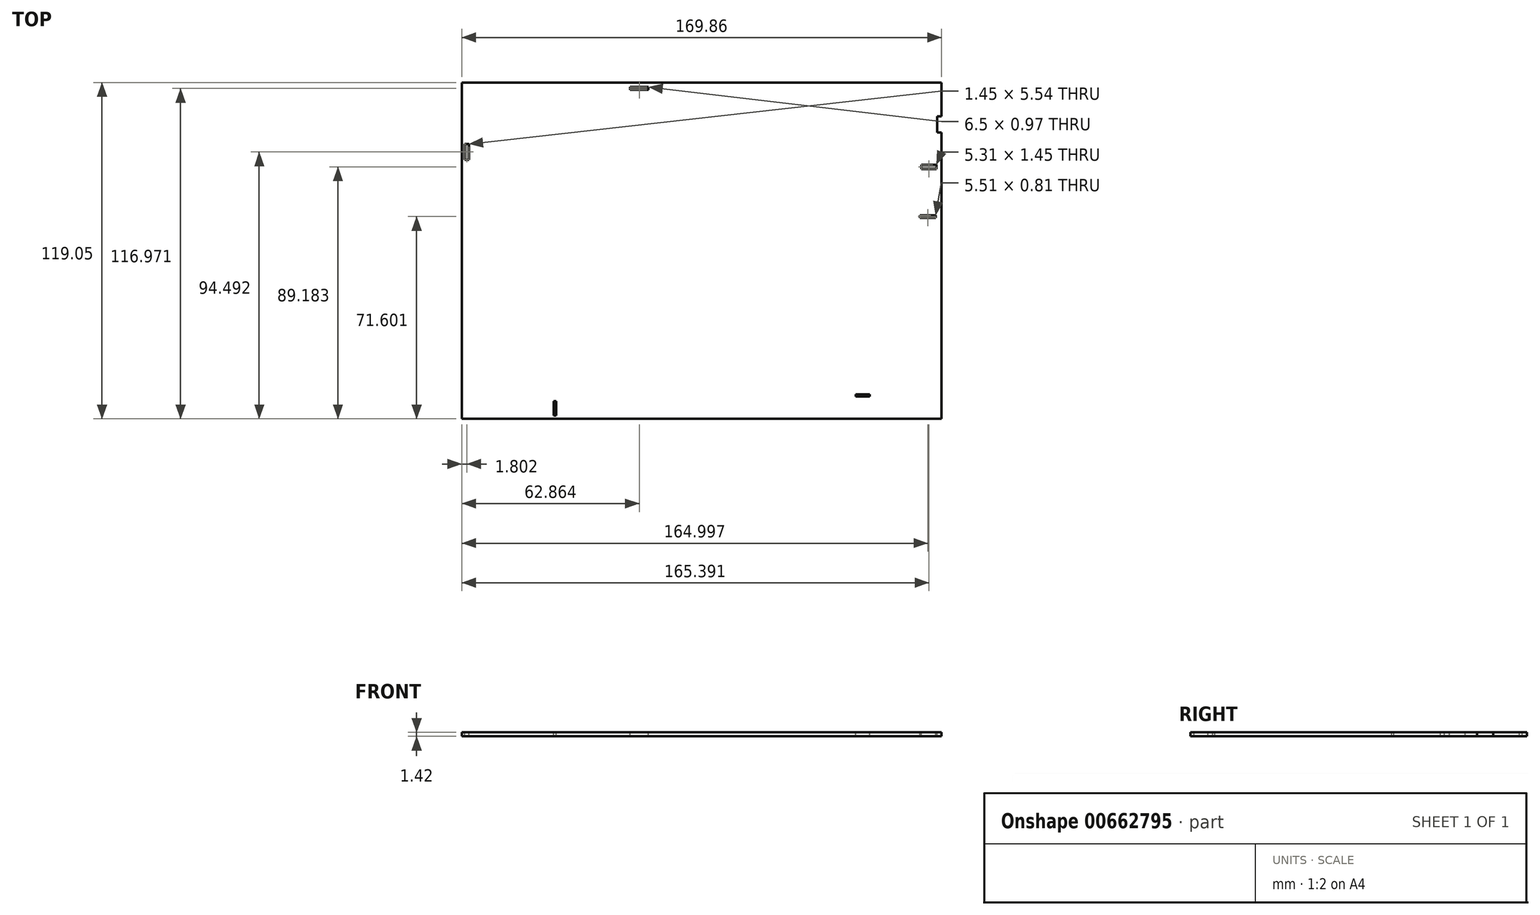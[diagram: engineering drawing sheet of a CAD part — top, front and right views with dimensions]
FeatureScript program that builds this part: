
annotation { "Feature Type Name" : "Feature", "Feature Type Description" : "" }
export const myFeature = defineFeature(function(context is Context, id is Id, definition is map)
    precondition{}
    {
        {
            var Q0;
            Q0=qCreatedBy(makeId("Top.planeOp"),FACE);
            var sketch = newSketch(context, id + "F0", { "sketchPlane" : qUnion([Q0])});
            skLineSegment(sketch, "E0.bottom", {"start": v(-84.93, 66.54) * mm, "end": v(84.93, 66.54) * mm});
            skLineSegment(sketch, "E0.top", {"start": v(-84.93, -52.5) * mm, "end": v(84.93, -52.5) * mm});
            skLineSegment(sketch, "E0.left", {"start": v(-84.93, 66.54) * mm, "end": v(-84.93, -52.5) * mm});
            skLineSegment(sketch, "E0.right", {"start": v(84.93, 66.54) * mm, "end": v(84.93, -52.5) * mm});
            skSolve(sketch);
        }
        {
            var Q0;
            Q0=makeQuery(id+"F0.imprint","IMPRINT",FACE,{"disambiguationData":[TD([[makeQuery(id+"F0.imprint","IMPRINT",EDGE,{"derivedFrom":sQuery(id+"F0.wireOp",EDGE,"E0.bottom")}),-1.0]])]});
            extrude(context, id + "F1", {"entities" : qUnion([Q0]), "depth" : 1.42 * mm, "offsetDistance" : 25.4 * mm});
        }
        {
            var Q0;
            Q0=makeQuery(id+"F1.opExtrude","CAP_FACE",FACE,{"disambiguationData":[OSD([sQuery(id+"F0.wireOp",EDGE,"E0.bottom"),sQuery(id+"F0.wireOp",EDGE,"E0.top"),sQuery(id+"F0.wireOp",EDGE,"E0.left"),sQuery(id+"F0.wireOp",EDGE,"E0.right")])],"isStart":false});
            var sketch = newSketch(context, id + "F2", { "sketchPlane" : qUnion([Q0])});
            skLineSegment(sketch, "E1", {"start": v(80.33, -52.5) * mm, "end": v(80.33, -45.01) * mm});
            skLineSegment(sketch, "E2", {"start": v(84.93, -45.01) * mm, "end": v(80.33, -45.01) * mm});
            skLineSegment(sketch, "E3", {"start": v(84.93, -44.23) * mm, "end": v(57, -44.23) * mm});
            skPoint(sketch, "E3.startSnap0", {"position": v(80.33, -44.23) * mm});
            skLineSegment(sketch, "E4", {"start": v(57, -44.23) * mm, "end": v(57, -52.5) * mm});
            skLineSegment(sketch, "E5.bottom", {"start": v(59.48, -43.83) * mm, "end": v(54.5, -43.83) * mm});
            skLineSegment(sketch, "E5.top", {"start": v(59.48, -44.62) * mm, "end": v(54.5, -44.62) * mm});
            skLineSegment(sketch, "E5.left", {"start": v(59.48, -43.83) * mm, "end": v(59.48, -44.62) * mm});
            skLineSegment(sketch, "E5.right", {"start": v(54.5, -43.83) * mm, "end": v(54.5, -44.62) * mm});
            skPoint(sketch, "E5.middle", {"position": v(57, -44.23) * mm});
            skLineSegment(sketch, "E6", {"start": v(-84.93, -48.8) * mm, "end": v(-51.91, -48.8) * mm});
            skLineSegment(sketch, "E7", {"start": v(-51.91, -48.8) * mm, "end": v(-51.91, -52.5) * mm});
            skLineSegment(sketch, "E8.bottom", {"start": v(-51.45, -51.31) * mm, "end": v(-52.37, -51.31) * mm});
            skLineSegment(sketch, "E8.top", {"start": v(-51.45, -46.28) * mm, "end": v(-52.37, -46.28) * mm});
            skLineSegment(sketch, "E8.left", {"start": v(-51.45, -51.31) * mm, "end": v(-51.45, -46.28) * mm});
            skLineSegment(sketch, "E8.right", {"start": v(-52.37, -51.31) * mm, "end": v(-52.37, -46.28) * mm});
            skPoint(sketch, "E8.middle", {"position": v(-51.91, -48.8) * mm});
            skLineSegment(sketch, "E9", {"start": v(-83.13, 66.54) * mm, "end": v(-83.13, 41.98) * mm});
            skLineSegment(sketch, "E10", {"start": v(-83.13, 41.98) * mm, "end": v(-84.93, 41.98) * mm});
            skLineSegment(sketch, "E11.bottom", {"start": v(-82.4, 39.21) * mm, "end": v(-83.85, 39.21) * mm});
            skLineSegment(sketch, "E11.top", {"start": v(-82.4, 44.75) * mm, "end": v(-83.85, 44.75) * mm});
            skLineSegment(sketch, "E11.left", {"start": v(-82.4, 39.21) * mm, "end": v(-82.4, 44.75) * mm});
            skLineSegment(sketch, "E11.right", {"start": v(-83.85, 39.21) * mm, "end": v(-83.85, 44.75) * mm});
            skPoint(sketch, "E11.middle", {"position": v(-83.13, 41.98) * mm});
            skLineSegment(sketch, "E12", {"start": v(-84.93, 64.46) * mm, "end": v(-22.07, 64.46) * mm});
            skLineSegment(sketch, "E13", {"start": v(-22.07, 64.46) * mm, "end": v(-22.07, 66.54) * mm});
            skLineSegment(sketch, "E14.bottom", {"start": v(-18.82, 63.98) * mm, "end": v(-25.32, 63.98) * mm});
            skLineSegment(sketch, "E14.top", {"start": v(-18.82, 64.94) * mm, "end": v(-25.32, 64.94) * mm});
            skLineSegment(sketch, "E14.left", {"start": v(-18.82, 63.98) * mm, "end": v(-18.82, 64.94) * mm});
            skLineSegment(sketch, "E14.right", {"start": v(-25.32, 63.98) * mm, "end": v(-25.32, 64.94) * mm});
            skPoint(sketch, "E14.middle", {"position": v(-22.07, 64.46) * mm});
            skLineSegment(sketch, "E15", {"start": v(84.83, 66.54) * mm, "end": v(84.83, 51.76) * mm});
            skLineSegment(sketch, "E16.bottom", {"start": v(86.3, 48.9) * mm, "end": v(83.36, 48.9) * mm});
            skLineSegment(sketch, "E16.top", {"start": v(86.3, 54.63) * mm, "end": v(83.36, 54.63) * mm});
            skLineSegment(sketch, "E16.left", {"start": v(86.3, 48.9) * mm, "end": v(86.3, 54.63) * mm});
            skLineSegment(sketch, "E16.right", {"start": v(83.36, 48.9) * mm, "end": v(83.36, 54.63) * mm});
            skPoint(sketch, "E16.middle", {"position": v(84.83, 51.76) * mm});
            skLineSegment(sketch, "E17", {"start": v(80.46, 66.54) * mm, "end": v(80.46, 36.67) * mm});
            skLineSegment(sketch, "E18", {"start": v(84.93, 36.67) * mm, "end": v(80.46, 36.67) * mm});
            skLineSegment(sketch, "E19.bottom", {"start": v(83.12, 35.95) * mm, "end": v(77.8, 35.95) * mm});
            skLineSegment(sketch, "E19.top", {"start": v(83.12, 37.4) * mm, "end": v(77.8, 37.4) * mm});
            skLineSegment(sketch, "E19.left", {"start": v(83.12, 35.95) * mm, "end": v(83.12, 37.4) * mm});
            skLineSegment(sketch, "E19.right", {"start": v(77.8, 35.95) * mm, "end": v(77.8, 37.4) * mm});
            skPoint(sketch, "E19.middle", {"position": v(80.46, 36.67) * mm});
            skLineSegment(sketch, "E20", {"start": v(82.82, 66.54) * mm, "end": v(82.82, 19.17) * mm});
            skLineSegment(sketch, "E21", {"start": v(82.82, 19.17) * mm, "end": v(84.93, 19.17) * mm});
            skLineSegment(sketch, "E22.bottom", {"start": v(82.82, 19.5) * mm, "end": v(77.31, 19.5) * mm});
            skLineSegment(sketch, "E22.top", {"start": v(82.82, 18.68) * mm, "end": v(77.31, 18.68) * mm});
            skLineSegment(sketch, "E22.left", {"start": v(82.82, 19.5) * mm, "end": v(82.82, 18.68) * mm});
            skLineSegment(sketch, "E22.right", {"start": v(77.31, 19.5) * mm, "end": v(77.31, 18.68) * mm});
            skSolve(sketch);
        }
        {
            var Q0;
            Q0 = qSketchRegion(id + "F2", true);
            extrude(context, id + "F3", {"entities" : qUnion([Q0]), "operationType" : NewBodyOperationType.REMOVE, "oppositeDirection" : true, "depth" : 25.4 * mm, "offsetDistance" : 25.4 * mm});
        }
    });
